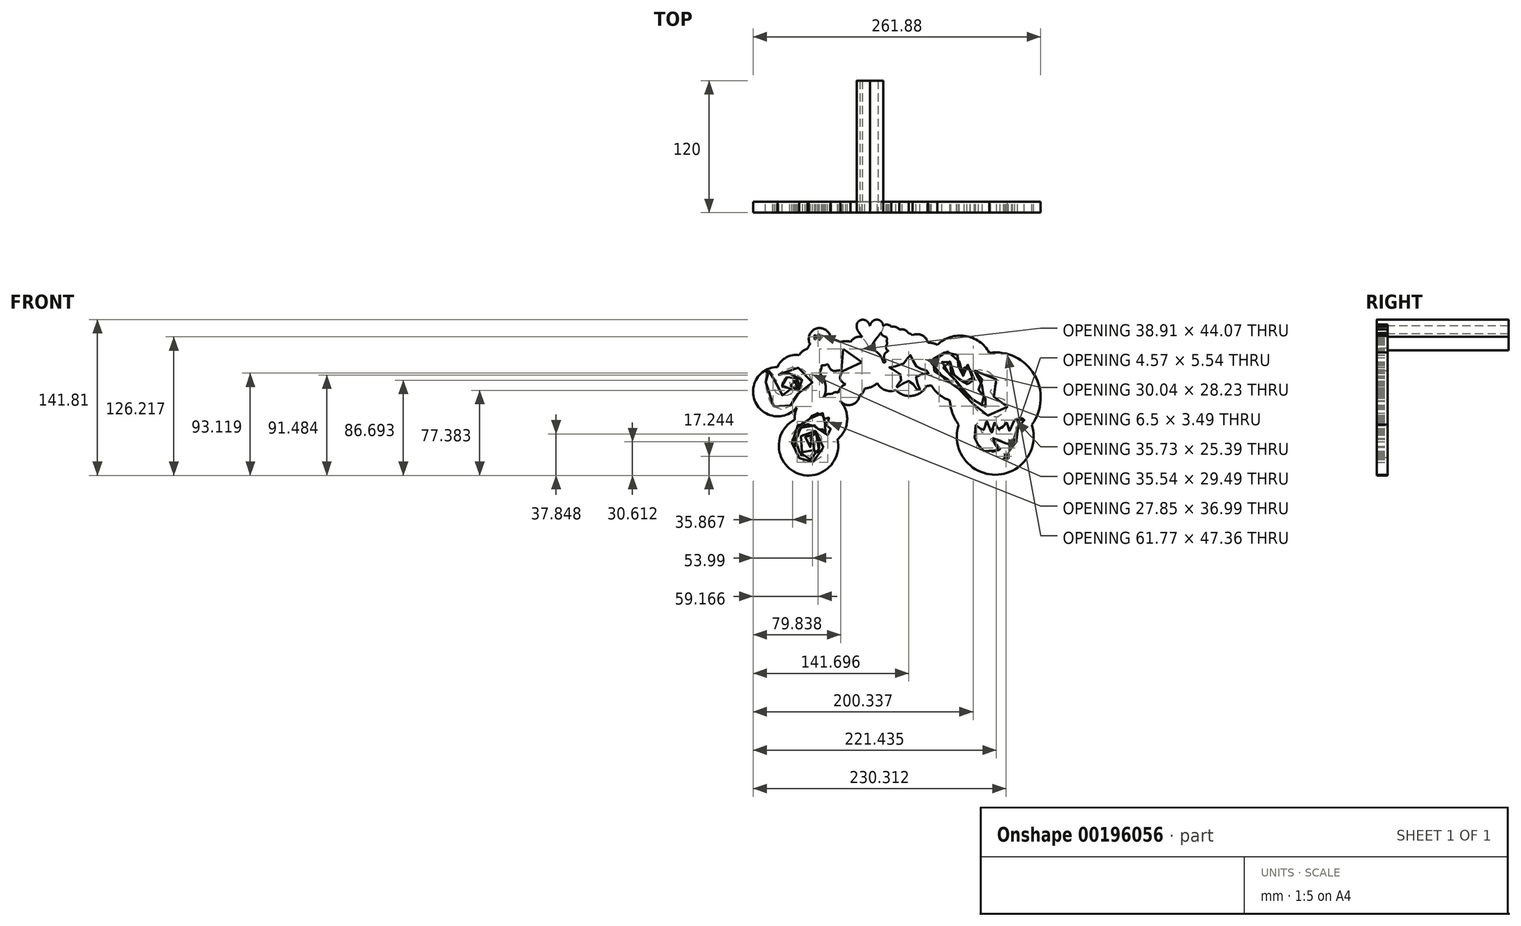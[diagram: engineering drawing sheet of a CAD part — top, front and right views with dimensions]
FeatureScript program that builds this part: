
annotation { "Feature Type Name" : "Feature", "Feature Type Description" : "" }
export const myFeature = defineFeature(function(context is Context, id is Id, definition is map)
    precondition{}
    {
        {
            var Q0;
            Q0=qCreatedBy(makeId("Front.planeOp"),FACE);
            var sketch = newSketch(context, id + "F0", { "sketchPlane" : qUnion([Q0])});
            skArc(sketch, "E0", {"start": v(-68.84, -80.9) * mm, "mid": v(-67.39, -129.26) * mm, "end": v(-29.77, -98.83) * mm});
            skArc(sketch, "E1", {"start": v(80.5, -85.48) * mm, "mid": v(113.88, -131.04) * mm, "end": v(147.25, -85.48) * mm});
            skArc(sketch, "E2", {"start": v(-29.77, -98.83) * mm, "mid": v(-20.94, -82.02) * mm, "end": v(-27.1, -64.06) * mm});
            skArc(sketch, "E3", {"start": v(72.58, -63.4) * mm, "mid": v(74.94, -75.01) * mm, "end": v(80.5, -85.48) * mm});
            skArc(sketch, "E4", {"start": v(55.8, -49.75) * mm, "mid": v(62.93, -58.12) * mm, "end": v(72.58, -63.4) * mm});
            skArc(sketch, "E5", {"start": v(-67.31, -70.3) * mm, "mid": v(-67.06, -70.4) * mm, "end": v(-66.8, -70.5) * mm});
            skArc(sketch, "E6", {"start": v(51.48, -50.1) * mm, "mid": v(53.65, -50.04) * mm, "end": v(55.8, -49.75) * mm});
            skArc(sketch, "E7", {"start": v(23.46, -54.06) * mm, "mid": v(38.48, -59.2) * mm, "end": v(51.48, -50.1) * mm});
            skArc(sketch, "E8", {"start": v(6.42, -47.67) * mm, "mid": v(13.73, -54.1) * mm, "end": v(23.46, -54.06) * mm});
            skArc(sketch, "E9", {"start": v(-36.03, -8.26) * mm, "mid": v(-48.03, 2.25) * mm, "end": v(-54.7, -12.24) * mm});
            skArc(sketch, "E10", {"start": v(-17.78, -10.06) * mm, "mid": v(-22.48, -9.52) * mm, "end": v(-27.16, -10.28) * mm});
            skArc(sketch, "E11", {"start": v(-27.1, -64.06) * mm, "mid": v(-27.05, -64) * mm, "end": v(-27.01, -63.95) * mm});
            skArc(sketch, "E12", {"start": v(-9.7, -58.94) * mm, "mid": v(-6.6, -56.29) * mm, "end": v(-5.02, -52.54) * mm});
            skArc(sketch, "E13", {"start": v(-27.01, -63.95) * mm, "mid": v(-16.66, -67.3) * mm, "end": v(-9.7, -58.94) * mm});
            skPoint(sketch, "E14.center.orphan", {"position": v(-44.86, -56.2) * mm});
            skArc(sketch, "E15.trimOffspring", {"start": v(-42.26, -60.63) * mm, "mid": v(-40.66, -48.8) * mm, "end": v(-46.25, -38.23) * mm});
            skArc(sketch, "E16.trimOffspring", {"start": v(-34.98, -57.68) * mm, "mid": v(-39.15, -57.85) * mm, "end": v(-42.26, -60.63) * mm});
            skArc(sketch, "E17.trimOffspring", {"start": v(-28.96, -56.47) * mm, "mid": v(-32.17, -56.06) * mm, "end": v(-34.98, -57.68) * mm});
            skArc(sketch, "E18.trimOffspring", {"start": v(-22.35, -48.72) * mm, "mid": v(-26.75, -51.66) * mm, "end": v(-28.96, -56.47) * mm});
            skArc(sketch, "E19.trimOffspring", {"start": v(-5.02, -52.54) * mm, "mid": v(1.11, -51.07) * mm, "end": v(6.42, -47.67) * mm});
            skArc(sketch, "E20.trimOffspring", {"start": v(-44.15, -31.58) * mm, "mid": v(-41.46, -31.32) * mm, "end": v(-38.86, -30.54) * mm});
            skArc(sketch, "E21.trimOffspring", {"start": v(-64.55, -22.2) * mm, "mid": v(-76.3, -24.2) * mm, "end": v(-84.31, -33.02) * mm});
            skArc(sketch, "E22.trimOffspring", {"start": v(-46.25, -38.23) * mm, "mid": v(-44.68, -35.07) * mm, "end": v(-44.15, -31.58) * mm});
            skArc(sketch, "E23.trimOffspring", {"start": v(-56.92, -16.33) * mm, "mid": v(-61.38, -18.43) * mm, "end": v(-64.55, -22.2) * mm});
            skArc(sketch, "E24.trimOffspring", {"start": v(-54.7, -12.24) * mm, "mid": v(-56.02, -14.17) * mm, "end": v(-56.92, -16.33) * mm});
            skArc(sketch, "E25.trimOffspring", {"start": v(-27.16, -10.28) * mm, "mid": v(-31.42, -8.5) * mm, "end": v(-36.03, -8.26) * mm});
            skArc(sketch, "E26.trimOffspring", {"start": v(12.12, -29.2) * mm, "mid": v(7.77, -20.93) * mm, "end": v(0, -15.75) * mm});
            skArc(sketch, "E27.trimOffspring", {"start": v(61.03, -12.85) * mm, "mid": v(56.87, -11.28) * mm, "end": v(52.46, -10.69) * mm});
            skArc(sketch, "E28.trimOffspring", {"start": v(108.52, -20.02) * mm, "mid": v(86.54, -4.72) * mm, "end": v(61.03, -12.85) * mm});
            skArc(sketch, "E29.trimOffspring", {"start": v(147.25, -85.48) * mm, "mid": v(149.48, -39.97) * mm, "end": v(108.52, -20.02) * mm});
            skArc(sketch, "E30", {"start": v(0, -15.75) * mm, "mid": v(-6.63, -5.83) * mm, "end": v(-17.78, -10.06) * mm});
            skArc(sketch, "E31", {"start": v(31.14, -13.64) * mm, "mid": v(32.07, -14.07) * mm, "end": v(33.06, -14.33) * mm});
            skArc(sketch, "E32", {"start": v(19.36, 3.5) * mm, "mid": v(10.1, 2.57) * mm, "end": v(14.64, -5.55) * mm});
            skArc(sketch, "E33", {"start": v(16.47, -18.67) * mm, "mid": v(12.63, -22.84) * mm, "end": v(14.38, -28.24) * mm});
            skArc(sketch, "E34", {"start": v(19.39, -18.56) * mm, "mid": v(19.4, -18.3) * mm, "end": v(19.35, -18.06) * mm});
            skArc(sketch, "E35.trimOffspring", {"start": v(16.48, -18.17) * mm, "mid": v(16.45, -18.42) * mm, "end": v(16.47, -18.67) * mm});
            skArc(sketch, "E36.trimOffspring", {"start": v(15.58, -12.26) * mm, "mid": v(14.35, -15.47) * mm, "end": v(16.48, -18.17) * mm});
            skArc(sketch, "E37.trimOffspring", {"start": v(15.58, -10.68) * mm, "mid": v(15.42, -11.47) * mm, "end": v(15.58, -12.26) * mm});
            skArc(sketch, "E38.trimOffspring", {"start": v(14.38, -28.24) * mm, "mid": v(13.23, -28.67) * mm, "end": v(12.12, -29.2) * mm});
            skArc(sketch, "E39.trimOffspring", {"start": v(15.62, -7.41) * mm, "mid": v(14.96, -9.04) * mm, "end": v(15.58, -10.68) * mm});
            skArc(sketch, "E40.trimOffspring", {"start": v(14.64, -5.55) * mm, "mid": v(15.06, -6.52) * mm, "end": v(15.62, -7.41) * mm});
            skArc(sketch, "E41.trimOffspring", {"start": v(26.67, 1.2) * mm, "mid": v(23.36, 3.44) * mm, "end": v(19.36, 3.5) * mm});
            skArc(sketch, "E42.trimOffspring", {"start": v(34.97, -2.31) * mm, "mid": v(31.38, 0.77) * mm, "end": v(26.67, 1.2) * mm});
            skArc(sketch, "E43.trimOffspring", {"start": v(38.5, -4.1) * mm, "mid": v(36.88, -2.91) * mm, "end": v(34.97, -2.31) * mm});
            skArc(sketch, "E44.trimOffspring", {"start": v(52.46, -10.69) * mm, "mid": v(47.06, -4.03) * mm, "end": v(38.5, -4.1) * mm});
            skArc(sketch, "E45.trimOffspring", {"start": v(-84.31, -33.02) * mm, "mid": v(-104.6, -64.79) * mm, "end": v(-67.31, -70.3) * mm});
            skArc(sketch, "E46.trimOffspring", {"start": v(-66.8, -70.5) * mm, "mid": v(-68.4, -75.58) * mm, "end": v(-68.84, -80.9) * mm});
            skFitSpline(sketch, "E47", {"points": [v(-22.35, -48.72) * mm, v(-24.81, -36.03) * mm, v(-34.54, -36.13) * mm, v(-38.86, -30.54) * mm], "startDerivative": vector(-77.22, 36.92) * mm, "endDerivative": vector(-15.04, 5.46) * mm});
            skFitSpline(sketch, "E48", {"points": [v(94.68, -36.26) * mm, v(103.47, -35.69) * mm, v(114.12, -42.8) * mm, v(114.1, -50.02) * mm, v(108.9, -54.2) * mm, v(113.88, -61.04) * mm, v(117.17, -61.04) * mm, v(122.83, -63.35) * mm, v(124.19, -71.85) * mm, v(114.54, -78.87) * mm, v(107.55, -77.23) * mm, v(99.16, -74.05) * mm, v(95.25, -68.84) * mm, v(92.18, -64.93) * mm, v(88.05, -61.04) * mm, v(83.9, -56.93) * mm, v(78.6, -50.17) * mm, v(76.09, -47.05) * mm, v(71.2, -44.8) * mm, v(63.08, -41.35) * mm, v(55.3, -32.26) * mm, v(54.7, -30.41) * mm, v(59.78, -22.75) * mm, v(61.88, -21.61) * mm, v(69.54, -19.21) * mm, v(76.71, -18.17) * mm, v(80.39, -24.19) * mm, v(81.06, -28.17) * mm, v(80.63, -31.4) * mm, v(78.58, -33.87) * mm, v(82.53, -40.15) * mm, v(87.88, -40.5) * mm, v(86.08, -34.68) * mm, v(85.76, -33.09) * mm, v(89.69, -30.82) * mm, v(90.86, -33.72) * mm, v(91.28, -38.24) * mm, v(91.37, -40.91) * mm, v(95.8, -45.57) * mm, v(94.83, -48.54) * mm, v(89.23, -48.74) * mm, v(84.36, -46.76) * mm, v(83.82, -46.78) * mm, v(81.06, -44.2) * mm, v(77.76, -41.11) * mm, v(76.66, -40.35) * mm, v(73.37, -37.79) * mm, v(72.94, -33) * mm, v(73.4, -30.84) * mm, v(71.93, -26.88) * mm, v(68.92, -24.58) * mm, v(65.33, -28.98) * mm, v(66.55, -33.48) * mm, v(70.7, -37.88) * mm, v(72.12, -40.24) * mm, v(75.16, -43.34) * mm, v(78.99, -45.88) * mm, v(82.05, -49.52) * mm, v(85.71, -55.27) * mm, v(89.33, -61.04) * mm, v(95.34, -63.76) * mm, v(100.26, -67.06) * mm, v(107.27, -68.96) * mm, v(108.52, -66.51) * mm, v(104.36, -61.04) * mm, v(101.05, -58.75) * mm, v(98.52, -55.1) * mm, v(100.52, -51.02) * mm, v(101.8, -49.37) * mm, v(101.86, -43.23) * mm, v(98.24, -38.8) * mm, v(94.68, -36.26) * mm]});
            skFitSpline(sketch, "E49", {"points": [v(-66.57, -88.34) * mm, v(-68.36, -92.36) * mm, v(-71.16, -93.9) * mm, v(-69.6, -97) * mm, v(-71.1, -101.9) * mm, v(-70.34, -105.25) * mm, v(-68.36, -107.34) * mm, v(-67.33, -111.82) * mm, v(-65.1, -115.17) * mm, v(-63, -118) * mm, v(-60.73, -119.09) * mm, v(-57.94, -119.78) * mm, v(-55.27, -119.67) * mm, v(-51.4, -119.18) * mm, v(-46.16, -116.43) * mm, v(-44.27, -114.04) * mm, v(-43.29, -108.85) * mm, v(-42.7, -104.05) * mm, v(-43.84, -97.77) * mm, v(-45.81, -94.28) * mm, v(-48.59, -91.85) * mm, v(-51.38, -90.5) * mm, v(-53.9, -90.07) * mm, v(-57.65, -90.43) * mm, v(-62.1, -94.52) * mm, v(-63.18, -96.65) * mm, v(-64, -99.44) * mm, v(-64.18, -103.17) * mm, v(-63.4, -105.98) * mm, v(-62.03, -110.32) * mm, v(-59.59, -111.36) * mm, v(-55.35, -114.07) * mm, v(-52.68, -113.83) * mm, v(-51.44, -109.84) * mm, v(-50.2, -106.91) * mm, v(-49.35, -101.45) * mm, v(-50.1, -95.84) * mm, v(-52.09, -94.75) * mm, v(-55.02, -94.86) * mm, v(-57.45, -97.9) * mm, v(-55.75, -100.86) * mm, v(-54.44, -103.44) * mm, v(-54.6, -105.94) * mm, v(-55.04, -104.52) * mm, v(-56.12, -103) * mm, v(-56.12, -101.77) * mm, v(-58.68, -100.16) * mm, v(-59.2, -98.29) * mm, v(-58.9, -96.16) * mm, v(-56.12, -94.47) * mm, v(-56.35, -93.65) * mm, v(-54.6, -92.86) * mm, v(-52.47, -92.88) * mm, v(-50.2, -93.44) * mm, v(-47.7, -95.73) * mm, v(-46.93, -99.08) * mm, v(-46.81, -101.21) * mm, v(-46.57, -104.72) * mm, v(-46.74, -107.62) * mm, v(-47.7, -110.68) * mm, v(-50.34, -109.76) * mm, v(-51.23, -115.84) * mm, v(-53.64, -116.89) * mm, v(-56.12, -117.12) * mm, v(-57.95, -114.33) * mm, v(-60.64, -114.38) * mm, v(-62.41, -113.6) * mm, v(-64.26, -111.31) * mm, v(-64.92, -108.05) * mm, v(-67.54, -106.08) * mm, v(-68.07, -104.72) * mm, v(-68.7, -102.2) * mm, v(-68.7, -100.86) * mm, v(-67.2, -97.94) * mm, v(-66.52, -96.61) * mm, v(-65.29, -93.96) * mm, v(-65.15, -93.03) * mm, v(-65.12, -90.76) * mm, v(-62.83, -88.24) * mm, v(-60.54, -86.53) * mm, v(-60.27, -86.27) * mm, v(-56.12, -84.96) * mm, v(-55.47, -85.65) * mm, v(-53.2, -86.2) * mm, v(-51.2, -86.36) * mm, v(-50.13, -86.23) * mm, v(-46.48, -90.26) * mm, v(-43.76, -88.97) * mm, v(-41.66, -92.46) * mm, v(-38.88, -95.02) * mm, v(-36.97, -91.3) * mm, v(-36.41, -88.37) * mm, v(-41.33, -85) * mm, v(-37, -81.03) * mm, v(-38.19, -79.01) * mm, v(-42.63, -79.89) * mm, v(-43.08, -74.96) * mm, v(-44.62, -76.8) * mm, v(-47.75, -75.05) * mm, v(-50.17, -76.36) * mm, v(-53.65, -77.8) * mm, v(-56.12, -81.33) * mm, v(-60.91, -83.46) * mm, v(-63.66, -85.82) * mm, v(-65.74, -85.68) * mm, v(-66.57, -88.34) * mm]});
            skFitSpline(sketch, "E50", {"points": [v(-87.75, -69.08) * mm, v(-72.66, -68.03) * mm, v(-67.68, -58.76) * mm, v(-52.7, -47.95) * mm, v(-68.43, -33.25) * mm, v(-83.68, -40.78) * mm, v(-73.33, -38.74) * mm, v(-62.3, -43.76) * mm, v(-62.96, -52.5) * mm, v(-67.51, -54.98) * mm, v(-71.27, -52.3) * mm, v(-72.84, -46.15) * mm, v(-69.77, -45.78) * mm, v(-66.97, -46.47) * mm, v(-66.02, -50.15) * mm, v(-67.32, -50.04) * mm, v(-69.3, -50.62) * mm, v(-69.44, -52.5) * mm, v(-67.51, -53.03) * mm, v(-66.42, -52.91) * mm, v(-64.2, -50.73) * mm, v(-64.77, -45.3) * mm, v(-67.51, -43.2) * mm, v(-70.8, -43.1) * mm, v(-76.67, -42.5) * mm, v(-79.25, -46.49) * mm, v(-79.43, -51.55) * mm, v(-72.84, -52.53) * mm, v(-72.2, -57.64) * mm, v(-86.27, -55.47) * mm, v(-85.24, -45.05) * mm, v(-88.44, -43.82) * mm, v(-88.53, -40.26) * mm, v(-90.46, -38.13) * mm, v(-92.77, -36.4) * mm, v(-94.74, -38.6) * mm, v(-87.75, -69.08) * mm]});
            skFitSpline(sketch, "E51", {"points": [v(131.33, -81.18) * mm, v(126.36, -91.38) * mm, v(123.18, -81.59) * mm, v(118.8, -92.12) * mm, v(113.82, -82.64) * mm, v(110.65, -92.53) * mm, v(105.66, -81.96) * mm, v(102.2, -93.32) * mm, v(98.07, -84) * mm, v(94.8, -95.62) * mm, v(97.85, -102.55) * mm, v(100.86, -108.59) * mm, v(118.33, -107.34) * mm, v(109.8, -99.36) * mm, v(115.67, -98.3) * mm, v(129.49, -104.88) * mm, v(128.95, -98.43) * mm, v(134.15, -100.96) * mm, v(131.76, -93.94) * mm, v(140.2, -81.56) * mm, v(131.33, -81.18) * mm]});
            skFitSpline(sketch, "E52", {"points": [v(30.4, -29.92) * mm, v(36.42, -22.04) * mm, v(41.64, -31.9) * mm, v(48.68, -35.22) * mm, v(53.41, -38.46) * mm, v(42.04, -41.59) * mm, v(45.19, -53.56) * mm, v(43.13, -53.92) * mm, v(35.39, -45.7) * mm, v(25.1, -51.42) * mm, v(23.5, -51.33) * mm, v(28.93, -41.73) * mm, v(17.37, -33.46) * mm, v(30.4, -29.92) * mm]});
            skCircle(sketch, "E53.cCircle", {"center": v(-19.52, -27.63) * mm, "radius": 6.11 * mm, "construction": true});
            skLineSegment(sketch, "E53.0", {"start": v(-24.72, -16.57) * mm, "end": v(-7.34, -28.65) * mm});
            skLineSegment(sketch, "E53.1", {"start": v(-7.34, -28.65) * mm, "end": v(-26.49, -37.66) * mm});
            skLineSegment(sketch, "E53.2", {"start": v(-26.49, -37.66) * mm, "end": v(-24.72, -16.57) * mm});
            skPoint(sketch, "E53.0.midPoint", {"position": v(-16.03, -22.6) * mm});
            skText(sketch, "E54", { "text": "♫", "fontName": "NotoSerif-Regular.ttf"});
            skFitSpline(sketch, "E55", {"points": [v(-49.28, -4.98) * mm, v(-50.57, -3.83) * mm, v(-50.13, -7.96) * mm, v(-48.68, -6.25) * mm, v(-47.75, -6.2) * mm, v(-46.93, -6.96) * mm, v(-46.15, -8.41) * mm, v(-45.57, -7.39) * mm, v(-44.96, -6.72) * mm, v(-44.07, -5.73) * mm, v(-44.98, -4.68) * mm, v(-45.74, -4.08) * mm, v(-46.42, -3.6) * mm, v(-47.89, -3.64) * mm, v(-47.44, -4.9) * mm, v(-48.34, -5.33) * mm, v(-49.28, -4.98) * mm]});
            skFitSpline(sketch, "E56", {"points": [v(-45.52, -4.9) * mm, v(-45.8, -5.67) * mm, v(-45.54, -6.64) * mm, v(-46.34, -5.36) * mm, v(-45.52, -4.9) * mm]});
            skCircle(sketch, "E57", {"center": v(-45.1, -5.67) * mm, "radius": 0.26 * mm});
            const initialGuessF0  = {"E54": [0.12014, -0.11705, 1, 0, 0.0068]};
            skSetInitialGuess(sketch, initialGuessF0);
            skSolve(sketch);
        }
        {
            var Q0;
            Q0 = qSketchRegion(id + "F0", true);
            extrude(context, id + "F1", {"entities" : qUnion([Q0]), "depth" : 10 * mm});
        }
        {
            var Q0;
            Q0=makeQuery(id+"F1.opExtrude","CAP_FACE",FACE,{"disambiguationData":[OSD([sQuery(id+"F0.wireOp",EDGE,"E0"),sQuery(id+"F0.wireOp",EDGE,"E1"),sQuery(id+"F0.wireOp",EDGE,"E2"),sQuery(id+"F0.wireOp",EDGE,"E3"),sQuery(id+"F0.wireOp",EDGE,"E4"),sQuery(id+"F0.wireOp",EDGE,"yNtMTq7k-TVh5-S5j1-8que-8dEJqjcak5zO"),sQuery(id+"F0.wireOp",EDGE,"E5"),sQuery(id+"F0.wireOp",EDGE,"6GUepQoY-z8z7-SoFj-mdsd-NEOXVuxbvf2X"),sQuery(id+"F0.wireOp",EDGE,"E6"),sQuery(id+"F0.wireOp",EDGE,"E7"),sQuery(id+"F0.wireOp",EDGE,"E8"),sQuery(id+"F0.wireOp",EDGE,"9SHeAJ5n-tRro-U9oT-ov0Z-w02RL7oCX049"),sQuery(id+"F0.wireOp",EDGE,"E9"),sQuery(id+"F0.wireOp",EDGE,"E10"),sQuery(id+"F0.wireOp",EDGE,"E11"),sQuery(id+"F0.wireOp",EDGE,"E12"),sQuery(id+"F0.wireOp",EDGE,"E13"),sQuery(id+"F0.wireOp",EDGE,"b8f804b0-5e0a-4482-9c38-9eddef115d2d.trimOffspring"),sQuery(id+"F0.wireOp",EDGE,"8dc867ec-bd30-4430-875e-fe7fd2cda8ba.trimOffspring"),sQuery(id+"F0.wireOp",EDGE,"8512367a-1247-4dbe-b574-889f4ff4d16e.trimOffspring"),sQuery(id+"F0.wireOp",EDGE,"E15.trimOffspring"),sQuery(id+"F0.wireOp",EDGE,"ce04604c-c7a4-421b-a054-df82c28506b5.trimOffspring"),sQuery(id+"F0.wireOp",EDGE,"E16.trimOffspring"),sQuery(id+"F0.wireOp",EDGE,"E17.trimOffspring"),sQuery(id+"F0.wireOp",EDGE,"E18.trimOffspring"),sQuery(id+"F0.wireOp",EDGE,"E19.trimOffspring"),sQuery(id+"F0.wireOp",EDGE,"8a95e3bd-48b1-4c26-9de8-3a4db100e4e1.trimOffspring"),sQuery(id+"F0.wireOp",EDGE,"E20.trimOffspring"),sQuery(id+"F0.wireOp",EDGE,"E21.trimOffspring"),sQuery(id+"F0.wireOp",EDGE,"E22.trimOffspring"),sQuery(id+"F0.wireOp",EDGE,"fae8b6e0-2fc3-406a-a279-8dc4e94f99ed.trimOffspring"),sQuery(id+"F0.wireOp",EDGE,"E23.trimOffspring"),sQuery(id+"F0.wireOp",EDGE,"E24.trimOffspring"),sQuery(id+"F0.wireOp",EDGE,"E25.trimOffspring"),sQuery(id+"F0.wireOp",EDGE,"54d11123-9ce1-4462-8e2b-be4a70cd5647.trimOffspring"),sQuery(id+"F0.wireOp",EDGE,"E26.trimOffspring"),sQuery(id+"F0.wireOp",EDGE,"a922d502-5dd7-4bf3-9f3d-b3b087fae149.trimOffspring"),sQuery(id+"F0.wireOp",EDGE,"a97a461a-9095-49bd-a38c-ccfa5997f522.trimOffspring"),sQuery(id+"F0.wireOp",EDGE,"E27.trimOffspring"),sQuery(id+"F0.wireOp",EDGE,"E28.trimOffspring"),sQuery(id+"F0.wireOp",EDGE,"E29.trimOffspring")])],"isStart":false});
            var sketch = newSketch(context, id + "F2", { "sketchPlane" : qUnion([Q0])});
            skLineSegment(sketch, "E58", {"start": v(-62.2, -131.03) * mm, "end": v(112.94, -131.03) * mm});
            skText(sketch, "E59", { "text": "♥", "fontName": "Arimo-Regular.ttf"});
            const initialGuessF2  = {"E59": [-0.0148, -0.01724, 1, 0, 0.0352]};
            skSetInitialGuess(sketch, initialGuessF2);
            skSolve(sketch);
        }
        {
            var Q0;
            Q0 = qSketchRegion(id + "F2", true);
            extrude(context, id + "F3", {"entities" : qUnion([Q0]), "operationType" : NewBodyOperationType.ADD, "oppositeDirection" : true, "depth" : 120 * mm});
        }
    });
